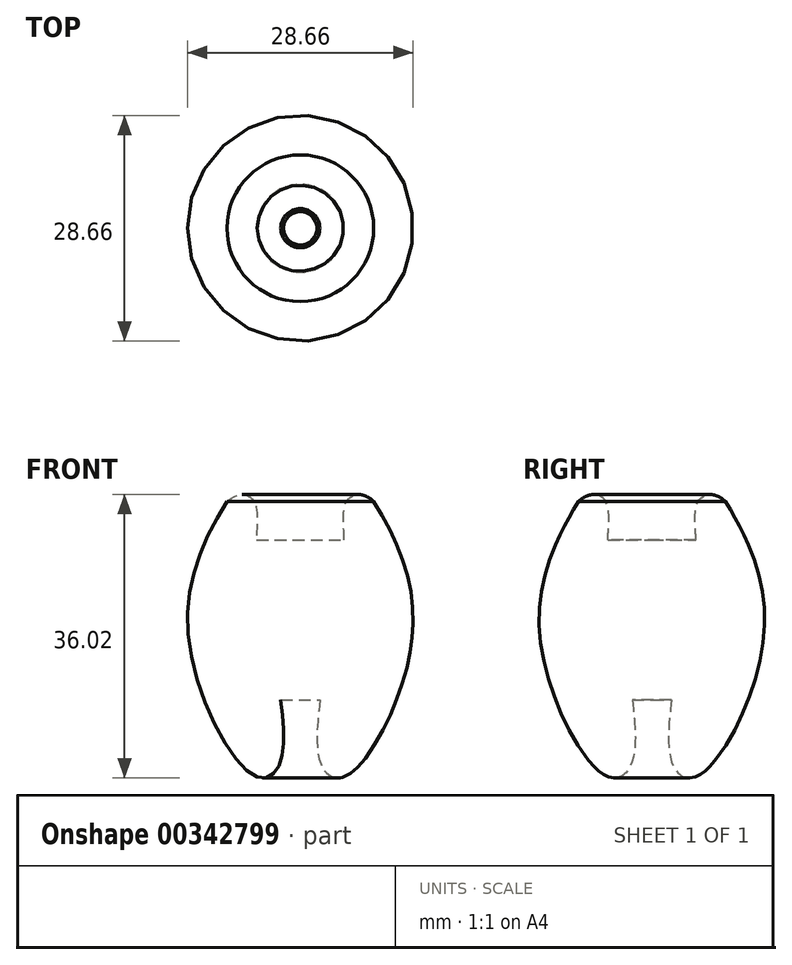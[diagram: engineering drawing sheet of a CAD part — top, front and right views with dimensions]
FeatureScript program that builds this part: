
annotation { "Feature Type Name" : "Feature", "Feature Type Description" : "" }
export const myFeature = defineFeature(function(context is Context, id is Id, definition is map)
    precondition{}
    {
        {
            var Q0;
            Q0=qCreatedBy(makeId("Front.planeOp"),FACE);
            var sketch = newSketch(context, id + "F0", { "sketchPlane" : qUnion([Q0])});
            skLineSegment(sketch, "E0", {"start": v(0, 82.52) * mm, "end": v(0, -99.27) * mm, "construction": true});
            skSolve(sketch);
        }
        {
            var Q0;
            Q0=qCreatedBy(makeId("Front.planeOp"),FACE);
            var sketch = newSketch(context, id + "F1", { "sketchPlane" : qUnion([Q0])});
            skFitSpline(sketch, "E1", {"points": [v(9.32, 15.03) * mm, v(14.1, -3.15) * mm, v(5.6, -19.97) * mm, v(2.7, -18.51) * mm, v(2.48, -10.2) * mm], "startDerivative": vector(30.91, -50.14) * mm, "endDerivative": vector(4.76, 44.16) * mm});
            skFitSpline(sketch, "E2", {"points": [v(9.32, 15.03) * mm, v(6.05, 15.25) * mm, v(5.49, 12.08) * mm, v(5.57, 10.1) * mm], "startDerivative": vector(-11.43, 10.1) * mm, "endDerivative": vector(-0.46, -5.5) * mm});
            skSolve(sketch);
        }
        {
            var Q0;
            Q0 = qSketchRegion(id + "F1", true);
            var Q1;
            Q1=sQuery(id+"F1.wireOp",EDGE,"E2");
            var Q2;
            Q2=sQuery(id+"F1.wireOp",EDGE,"E1");
            var Q3;
            Q3=sQuery(id+"F0.wireOp",EDGE,"E0");
            revolve(context, id + "F2", {"bodyType" : ToolBodyType.SURFACE, "entities" : qUnion([Q0]), "surfaceEntities" : qUnion([Q1, Q2]), "axis" : qUnion([Q3]), "revolveType" : RevolveType.FULL});
        }
    });
